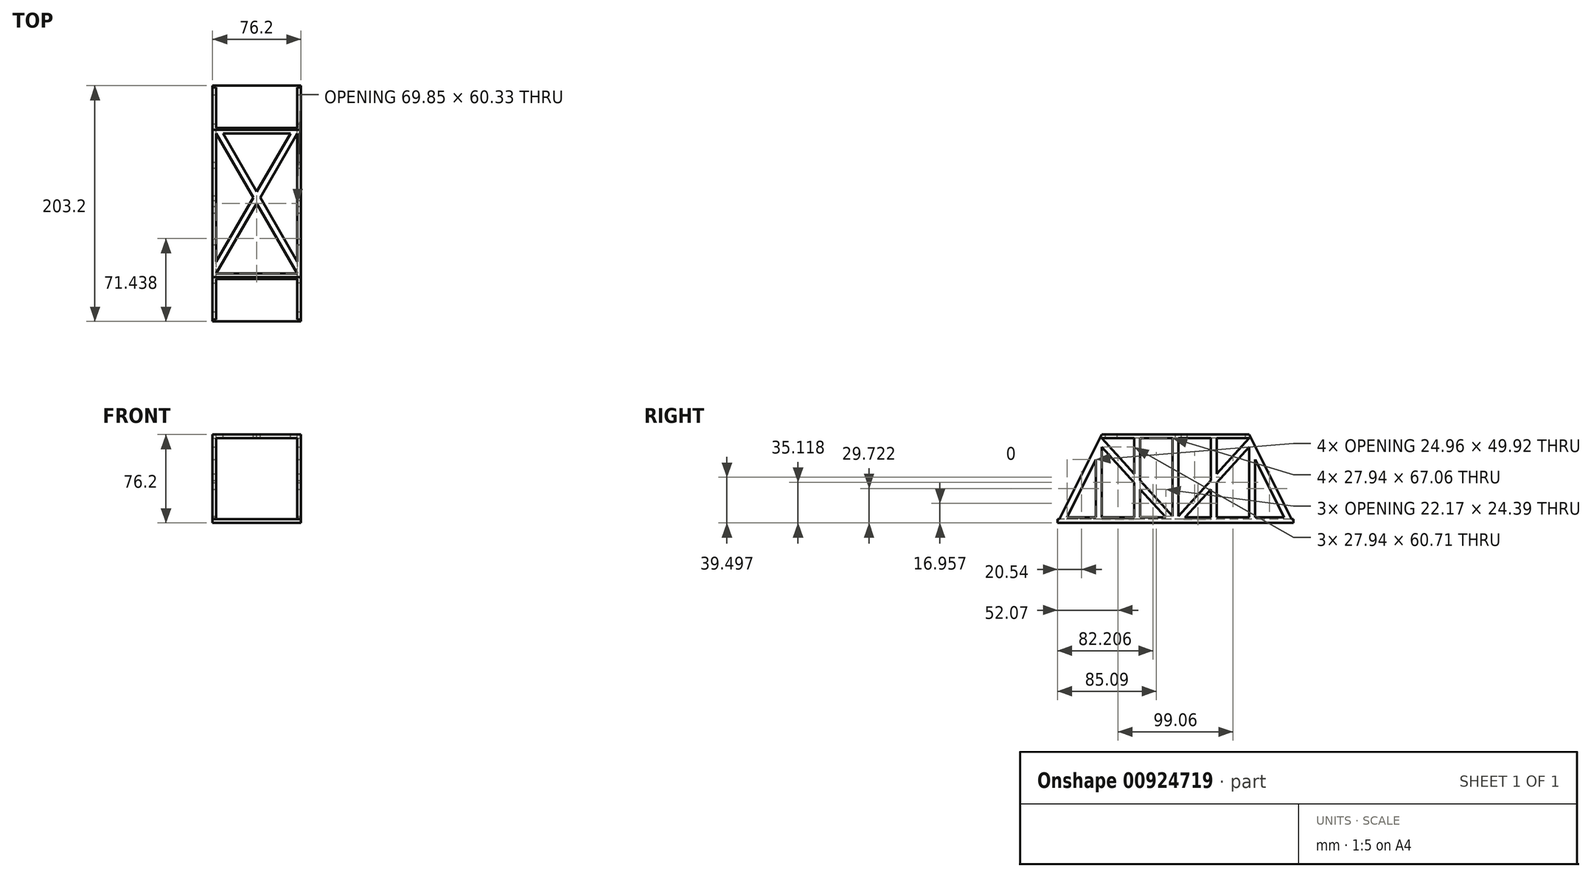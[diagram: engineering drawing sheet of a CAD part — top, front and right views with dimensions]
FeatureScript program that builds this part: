
annotation { "Feature Type Name" : "Feature", "Feature Type Description" : "" }
export const myFeature = defineFeature(function(context is Context, id is Id, definition is map)
    precondition{}
    {
        {
            var Q0;
            Q0=qCreatedBy(makeId("Right.planeOp"),FACE);
            var sketch = newSketch(context, id + "F0", { "sketchPlane" : qUnion([Q0])});
            skLineSegment(sketch, "E0", {"start": v(-101.6, -38.1) * mm, "end": v(101.6, -38.1) * mm});
            skLineSegment(sketch, "E1", {"start": v(-63.5, 38.1) * mm, "end": v(63.5, 38.1) * mm});
            skLineSegment(sketch, "E2", {"start": v(-101.6, -38.1) * mm, "end": v(-63.5, 38.1) * mm});
            skLineSegment(sketch, "E3", {"start": v(63.5, 38.1) * mm, "end": v(101.6, -38.1) * mm});
            skSolve(sketch);
        }
        {
            var Q0;
            Q0=qSketchRegion(id+"F0",true);
            extrude(context, id + "F1", {"entities" : qUnion([Q0]), "endBound" : BoundingType.SYMMETRIC, "depth" : 76.2 * mm, "offsetDistance" : 25.4 * mm});
        }
        {
            var Q0;
            Q0=makeQuery(id+"F1.opExtrude","CAP_FACE",FACE,{"disambiguationData":[OSD([sQuery(id+"F0.wireOp",EDGE,"E0"),sQuery(id+"F0.wireOp",EDGE,"E1"),sQuery(id+"F0.wireOp",EDGE,"E2"),sQuery(id+"F0.wireOp",EDGE,"E3")])],"isStart":false});
            var sketch = newSketch(context, id + "F2", { "sketchPlane" : qUnion([Q0])});
            skLineSegment(sketch, "E4", {"start": v(-63.5, 34.92) * mm, "end": v(-63.5, -34.93) * mm});
            skLineSegment(sketch, "E5", {"start": v(-63.5, -34.93) * mm, "end": v(63.5, -34.93) * mm});
            skLineSegment(sketch, "E6", {"start": v(63.5, -34.93) * mm, "end": v(63.5, 34.93) * mm});
            skLineSegment(sketch, "E7", {"start": v(63.5, 34.93) * mm, "end": v(-63.5, 34.92) * mm});
            skLineSegment(sketch, "E8", {"start": v(-63.5, 34.93) * mm, "end": v(0, -34.93) * mm});
            skLineSegment(sketch, "E9", {"start": v(0, -34.92) * mm, "end": v(63.5, 34.93) * mm});
            skLineSegment(sketch, "E10", {"start": v(-63.5, 27.37) * mm, "end": v(-6.87, -34.93) * mm});
            skLineSegment(sketch, "E11", {"start": v(63.5, 27.37) * mm, "end": v(6.87, -34.93) * mm});
            skLineSegment(sketch, "E12", {"start": v(-68.58, 16.58) * mm, "end": v(-68.58, -34.93) * mm});
            skLineSegment(sketch, "E13", {"start": v(-68.58, 16.58) * mm, "end": v(-94.33, -34.93) * mm});
            skLineSegment(sketch, "E14", {"start": v(-94.33, -34.93) * mm, "end": v(-68.58, -34.93) * mm});
            skLineSegment(sketch, "E15.MirrorCS", {"start": v(68.58, 16.58) * mm, "end": v(68.58, -34.93) * mm});
            skLineSegment(sketch, "E16.MirrorCS", {"start": v(68.58, 16.58) * mm, "end": v(94.33, -34.93) * mm});
            skLineSegment(sketch, "E17.MirrorCS", {"start": v(94.33, -34.93) * mm, "end": v(68.58, -34.93) * mm});
            skLineSegment(sketch, "E18.bottom", {"start": v(2.54, -34.93) * mm, "end": v(-2.54, -34.93) * mm});
            skLineSegment(sketch, "E18.top", {"start": v(2.54, 34.93) * mm, "end": v(-2.54, 34.93) * mm});
            skLineSegment(sketch, "E18.left", {"start": v(2.54, -34.92) * mm, "end": v(2.54, 34.92) * mm});
            skLineSegment(sketch, "E18.right", {"start": v(-2.54, -34.92) * mm, "end": v(-2.54, 34.92) * mm});
            skPoint(sketch, "E18.middle", {"position": v(0, 0) * mm});
            skLineSegment(sketch, "E19.bottom", {"start": v(-30.48, -34.93) * mm, "end": v(-35.56, -34.93) * mm});
            skLineSegment(sketch, "E19.top", {"start": v(-30.48, 34.93) * mm, "end": v(-35.56, 34.93) * mm});
            skLineSegment(sketch, "E19.left", {"start": v(-30.48, -34.93) * mm, "end": v(-30.48, 34.93) * mm});
            skLineSegment(sketch, "E19.right", {"start": v(-35.56, -34.93) * mm, "end": v(-35.56, 34.93) * mm});
            skPoint(sketch, "E19.middle", {"position": v(-33.02, 0) * mm});
            skLineSegment(sketch, "E20.MirrorCS", {"start": v(35.56, -34.93) * mm, "end": v(35.56, 34.93) * mm});
            skLineSegment(sketch, "E21.MirrorCS", {"start": v(30.48, -34.93) * mm, "end": v(30.48, 34.93) * mm});
            skSolve(sketch);
        }
        {
            var Q0;
            Q0=qCreatedBy(makeId("Front.planeOp"),FACE);
            var sketch = newSketch(context, id + "F3", { "sketchPlane" : qUnion([Q0])});
            skLineSegment(sketch, "E22.bottom", {"start": v(34.93, -34.93) * mm, "end": v(-34.93, -34.93) * mm});
            skLineSegment(sketch, "E22.top", {"start": v(34.93, 34.93) * mm, "end": v(-34.93, 34.93) * mm});
            skLineSegment(sketch, "E22.left", {"start": v(34.93, -34.93) * mm, "end": v(34.93, 34.93) * mm});
            skLineSegment(sketch, "E22.right", {"start": v(-34.93, -34.93) * mm, "end": v(-34.93, 34.93) * mm});
            skPoint(sketch, "E22.middle", {"position": v(0, 0) * mm});
            skSolve(sketch);
        }
        {
            var Q0;
            Q0=qSketchRegion(id+"F3",true);
            extrude(context, id + "F4", {"entities" : qUnion([Q0]), "operationType" : NewBodyOperationType.REMOVE, "endBound" : BoundingType.SYMMETRIC, "oppositeDirection" : true, "depth" : 254 * mm, "offsetDistance" : 25.4 * mm});
        }
        {
            var Q0;
            Q0=makeQuery(id+"F2.imprint","IMPRINT",FACE,{"disambiguationData":[TD([[makeQuery(id+"F2.imprint","IMPRINT",EDGE,{"derivedFrom":sQuery(id+"F2.wireOp",EDGE,"E12")}),-1.0]])]});
            var Q1;
            {var subQ3=sQuery(id+"F2.wireOp",EDGE,"E10");Q1=makeQuery(id+"F2.imprint","IMPRINT",FACE,{"disambiguationData":[TD([[makeQuery(id+"F2.imprint","IMPRINT",EDGE,{"derivedFrom":subQ3}),-1.0]])]});}
            var Q2;
            {var subQ0=sQuery(id+"F2.wireOp",EDGE,"E8");var subQ3=sQuery(id+"F2.wireOp",EDGE,"E18.right");var subQ5=makeQuery(id+"F2.imprint","INTERSECT",VERTEX,{"derivedFrom":[subQ0,subQ3]});Q2=makeQuery(id+"F2.imprint","IMPRINT",FACE,{"disambiguationData":[TD([[makeQuery(id+"F2.imprint","IMPRINT",EDGE,{"disambiguationData":[TD([[subQ5,1.0]])],"derivedFrom":subQ0}),1.0]])]});}
            var Q3;
            {var subQ0=sQuery(id+"F2.wireOp",EDGE,"E9");var subQ3=sQuery(id+"F2.wireOp",EDGE,"E18.left");var subQ5=makeQuery(id+"F2.imprint","INTERSECT",VERTEX,{"derivedFrom":[subQ0,subQ3]});Q3=makeQuery(id+"F2.imprint","IMPRINT",FACE,{"disambiguationData":[TD([[makeQuery(id+"F2.imprint","IMPRINT",EDGE,{"disambiguationData":[TD([[subQ5,-1.0]])],"derivedFrom":subQ0}),1.0]])]});}
            var Q4;
            {var subQ3=sQuery(id+"F2.wireOp",EDGE,"E11");Q4=makeQuery(id+"F2.imprint","IMPRINT",FACE,{"disambiguationData":[TD([[makeQuery(id+"F2.imprint","IMPRINT",EDGE,{"derivedFrom":subQ3}),1.0]])]});}
            var Q5;
            Q5=makeQuery(id+"F2.imprint","IMPRINT",FACE,{"disambiguationData":[TD([[makeQuery(id+"F2.imprint","IMPRINT",EDGE,{"derivedFrom":sQuery(id+"F2.wireOp",EDGE,"E15.MirrorCS")}),1.0]])]});
            var Q6;
            {var subQ0=sQuery(id+"F2.wireOp",EDGE,"E5");var subQ1=sQuery(id+"F2.wireOp",EDGE,"E4");var subQ2=makeQuery(id+"F2.imprint","INTERSECT",VERTEX,{"derivedFrom":[subQ1,subQ0]});Q6=makeQuery(id+"F2.imprint","IMPRINT",FACE,{"disambiguationData":[TD([[makeQuery(id+"F2.imprint","IMPRINT",EDGE,{"disambiguationData":[TD([[subQ2,1.0]])],"derivedFrom":subQ1}),1.0]])]});}
            var Q7;
            {var subQ0=sQuery(id+"F2.wireOp",EDGE,"E8");var subQ3=sQuery(id+"F2.wireOp",EDGE,"E19.right");var subQ5=makeQuery(id+"F2.imprint","INTERSECT",VERTEX,{"derivedFrom":[subQ0,subQ3]});Q7=makeQuery(id+"F2.imprint","IMPRINT",FACE,{"disambiguationData":[TD([[makeQuery(id+"F2.imprint","IMPRINT",EDGE,{"disambiguationData":[TD([[subQ5,1.0]])],"derivedFrom":subQ0}),1.0]])]});}
            var Q8;
            {var subQ1=sQuery(id+"F2.wireOp",EDGE,"E7");var subQ3=sQuery(id+"F2.wireOp",EDGE,"E20.MirrorCS");var subQ4=makeQuery(id+"F2.imprint","INTERSECT",VERTEX,{"derivedFrom":[subQ1,subQ3]});Q8=makeQuery(id+"F2.imprint","IMPRINT",FACE,{"disambiguationData":[TD([[makeQuery(id+"F2.imprint","IMPRINT",EDGE,{"disambiguationData":[TD([[subQ4,1.0]])],"derivedFrom":subQ3}),-1.0]])]});}
            var Q9;
            {var subQ0=sQuery(id+"F2.wireOp",EDGE,"E6");var subQ1=sQuery(id+"F2.wireOp",EDGE,"E5");var subQ2=makeQuery(id+"F2.imprint","INTERSECT",VERTEX,{"derivedFrom":[subQ1,subQ0]});Q9=makeQuery(id+"F2.imprint","IMPRINT",FACE,{"disambiguationData":[TD([[makeQuery(id+"F2.imprint","IMPRINT",EDGE,{"disambiguationData":[TD([[subQ2,1.0]])],"derivedFrom":subQ1}),1.0]])]});}
            extrude(context, id + "F5", {"entities" : qUnion([Q0, Q1, Q2, Q3, Q4, Q5, Q6, Q7, Q8, Q9]), "operationType" : NewBodyOperationType.REMOVE, "oppositeDirection" : true, "depth" : 101.6 * mm, "offsetDistance" : 25.4 * mm});
        }
        {
            var Q0;
            Q0=makeQuery(id+"F1.opExtrude","SWEPT_FACE",FACE,{"disambiguationData":[OSD([sQuery(id+"F0.wireOp",EDGE,"E1")])]});
            var sketch = newSketch(context, id + "F6", { "sketchPlane" : qUnion([Q0])});
            skLineSegment(sketch, "E23.bottom", {"start": v(34.92, -60.32) * mm, "end": v(-34.92, -60.32) * mm});
            skLineSegment(sketch, "E23.top", {"start": v(34.92, 60.33) * mm, "end": v(-34.92, 60.32) * mm});
            skLineSegment(sketch, "E23.left", {"start": v(34.92, -60.33) * mm, "end": v(34.92, 60.33) * mm});
            skLineSegment(sketch, "E23.right", {"start": v(-34.92, -60.33) * mm, "end": v(-34.92, 60.33) * mm});
            skPoint(sketch, "E23.middle", {"position": v(0, 0) * mm});
            skLineSegment(sketch, "E24", {"start": v(-34.92, 60.32) * mm, "end": v(34.92, -60.32) * mm});
            skLineSegment(sketch, "E25", {"start": v(34.92, 60.33) * mm, "end": v(-34.92, -60.32) * mm});
            skLineSegment(sketch, "E26", {"start": v(-34.92, -50.19) * mm, "end": v(29.06, 60.32) * mm});
            skLineSegment(sketch, "E27", {"start": v(-29.06, 60.33) * mm, "end": v(34.92, -50.19) * mm});
            skSolve(sketch);
        }
        {
            var Q0;
            {var subQ0=sQuery(id+"F6.wireOp",EDGE,"E26");var subQ1=sQuery(id+"F6.wireOp",EDGE,"E23.top");var subQ2=makeQuery(id+"F6.imprint","INTERSECT",VERTEX,{"derivedFrom":[subQ1,subQ0]});Q0=makeQuery(id+"F6.imprint","IMPRINT",FACE,{"disambiguationData":[TD([[makeQuery(id+"F6.imprint","IMPRINT",EDGE,{"disambiguationData":[TD([[subQ2,-1.0]])],"derivedFrom":subQ1}),1.0]])]});}
            var Q1;
            {var subQ1=sQuery(id+"F6.wireOp",EDGE,"E23.right");var subQ3=sQuery(id+"F6.wireOp",EDGE,"E26");var subQ4=makeQuery(id+"F6.imprint","INTERSECT",VERTEX,{"derivedFrom":[subQ1,subQ3]});Q1=makeQuery(id+"F6.imprint","IMPRINT",FACE,{"disambiguationData":[TD([[makeQuery(id+"F6.imprint","IMPRINT",EDGE,{"disambiguationData":[TD([[subQ4,-1.0]])],"derivedFrom":subQ3}),1.0]])]});}
            var Q2;
            {var subQ1=sQuery(id+"F6.wireOp",EDGE,"E23.left");var subQ3=sQuery(id+"F6.wireOp",EDGE,"E27");var subQ4=makeQuery(id+"F6.imprint","INTERSECT",VERTEX,{"derivedFrom":[subQ1,subQ3]});Q2=makeQuery(id+"F6.imprint","IMPRINT",FACE,{"disambiguationData":[TD([[makeQuery(id+"F6.imprint","IMPRINT",EDGE,{"disambiguationData":[TD([[subQ4,1.0]])],"derivedFrom":subQ3}),1.0]])]});}
            var Q3;
            {var subQ0=sQuery(id+"F6.wireOp",EDGE,"E23.bottom");Q3=makeQuery(id+"F6.imprint","IMPRINT",FACE,{"disambiguationData":[TD([[makeQuery(id+"F6.imprint","IMPRINT",EDGE,{"derivedFrom":subQ0}),-1.0]])]});}
            extrude(context, id + "F7", {"entities" : qUnion([Q0, Q1, Q2, Q3]), "operationType" : NewBodyOperationType.REMOVE, "oppositeDirection" : true, "depth" : 3.17 * mm, "offsetDistance" : 25.4 * mm});
        }
        {
            var Q0;
            {var subQ0=sQuery(id+"F2.wireOp",EDGE,"E5");Q0=makeQuery(id+"F5.boolean.opBoolean","MERGE",FACE,{"derivedFrom":[makeQuery(id+"F4.boolean.opBoolean","COPY",FACE,{"derivedFrom":makeQuery(id+"F4.opExtrude","SWEPT_FACE",FACE,{"disambiguationData":[OSD([sQuery(id+"F3.wireOp",EDGE,"E22.bottom")])]})})],"fromTools":[makeQuery(id+"F5.opExtrude","SWEPT_FACE",FACE,{"disambiguationData":[OSD([subQ0]),TDD([makeQuery(id+"F2.imprint","IMPRINT",EDGE,{"disambiguationData":[TD([[makeQuery(id+"F2.imprint","INTERSECT",VERTEX,{"derivedFrom":[sQuery(id+"F2.wireOp",EDGE,"E4"),subQ0]}),-1.0]])],"derivedFrom":subQ0})])]}),makeQuery(id+"F5.opExtrude","SWEPT_FACE",FACE,{"disambiguationData":[OSD([subQ0]),TDD([makeQuery(id+"F2.imprint","IMPRINT",EDGE,{"disambiguationData":[TD([[makeQuery(id+"F2.imprint","INTERSECT",VERTEX,{"derivedFrom":[subQ0,sQuery(id+"F2.wireOp",EDGE,"E6")]}),1.0]])],"derivedFrom":subQ0})])]}),makeQuery(id+"F5.opExtrude","SWEPT_FACE",FACE,{"disambiguationData":[OSD([sQuery(id+"F2.wireOp",EDGE,"E14")])]}),makeQuery(id+"F5.opExtrude","SWEPT_FACE",FACE,{"disambiguationData":[OSD([sQuery(id+"F2.wireOp",EDGE,"E17.MirrorCS")])]})]});}
            var sketch = newSketch(context, id + "F8", { "sketchPlane" : qUnion([Q0])});
            skLineSegment(sketch, "E28.bottom", {"start": v(38.1, -94.33) * mm, "end": v(34.92, -94.33) * mm});
            skLineSegment(sketch, "E28.top", {"start": v(38.1, 94.33) * mm, "end": v(34.92, 94.33) * mm});
            skLineSegment(sketch, "E28.left", {"start": v(38.1, -94.33) * mm, "end": v(38.1, 94.33) * mm});
            skLineSegment(sketch, "E28.right", {"start": v(34.92, -94.33) * mm, "end": v(34.92, 94.33) * mm});
            skLineSegment(sketch, "E29.MirrorCS", {"start": v(-38.1, -94.33) * mm, "end": v(-38.1, 94.33) * mm});
            skLineSegment(sketch, "E30.MirrorCS", {"start": v(-34.92, -94.33) * mm, "end": v(-34.92, 94.33) * mm});
            skSolve(sketch);
        }
        {
            var Q0;
            Q0=qSketchRegion(id+"F8",true);
            var Q1;
            {var subQ3=sQuery(id+"F3.wireOp",EDGE,"E22.right");var subQ4=makeQuery(id+"F4.boolean.opBoolean","COPY",FACE,{"derivedFrom":makeQuery(id+"F4.opExtrude","SWEPT_FACE",FACE,{"disambiguationData":[OSD([subQ3])]})});var subQ7=sQuery(id+"F2.wireOp",EDGE,"E12");var subQ11=sQuery(id+"F2.wireOp",EDGE,"E14");var subQ14=makeQuery(id+"F5.boolean.opBoolean","COPY",EDGE,{"disambiguationData":[TD([subQ4])],"derivedFrom":makeQuery(id+"F5.opExtrude","SWEPT_EDGE",EDGE,{"disambiguationData":[OSD([subQ7,subQ11])]})});Q1=makeQuery(id+"F8.imprint","IMPRINT",FACE,{"disambiguationData":[TD([[makeQuery(id+"F8.imprint","IMPRINT",EDGE,{"derivedFrom":subQ14}),-1.0]])]});}
            var Q2;
            {var subQ3=makeQuery(id+"F4.boolean.opBoolean","COPY",FACE,{"derivedFrom":makeQuery(id+"F4.opExtrude","SWEPT_FACE",FACE,{"disambiguationData":[OSD([sQuery(id+"F3.wireOp",EDGE,"E22.right")])]})});var subQ6=sQuery(id+"F2.wireOp",EDGE,"E5");var subQ7=sQuery(id+"F2.wireOp",EDGE,"E10");var subQ12=makeQuery(id+"F5.boolean.opBoolean","COPY",EDGE,{"disambiguationData":[TD([subQ3])],"derivedFrom":makeQuery(id+"F5.opExtrude","SWEPT_EDGE",EDGE,{"disambiguationData":[OSD([subQ6,subQ7])]})});Q2=makeQuery(id+"F8.imprint","IMPRINT",FACE,{"disambiguationData":[TD([[makeQuery(id+"F8.imprint","IMPRINT",EDGE,{"derivedFrom":subQ12}),-1.0]])]});}
            var Q3;
            {var subQ1=sQuery(id+"F2.wireOp",EDGE,"E5");var subQ3=makeQuery(id+"F4.boolean.opBoolean","COPY",FACE,{"derivedFrom":makeQuery(id+"F4.opExtrude","SWEPT_FACE",FACE,{"disambiguationData":[OSD([sQuery(id+"F3.wireOp",EDGE,"E22.right")])]})});var subQ5=sQuery(id+"F2.wireOp",EDGE,"E6");var subQ11=makeQuery(id+"F5.boolean.opBoolean","COPY",EDGE,{"disambiguationData":[TD([subQ3])],"derivedFrom":makeQuery(id+"F5.opExtrude","SWEPT_EDGE",EDGE,{"disambiguationData":[OSD([subQ1,subQ5])]})});Q3=makeQuery(id+"F8.imprint","IMPRINT",FACE,{"disambiguationData":[TD([[makeQuery(id+"F8.imprint","IMPRINT",EDGE,{"derivedFrom":subQ11}),-1.0]])]});}
            var Q4;
            {var subQ3=sQuery(id+"F3.wireOp",EDGE,"E22.right");var subQ4=makeQuery(id+"F4.boolean.opBoolean","COPY",FACE,{"derivedFrom":makeQuery(id+"F4.opExtrude","SWEPT_FACE",FACE,{"disambiguationData":[OSD([subQ3])]})});var subQ11=sQuery(id+"F2.wireOp",EDGE,"E15.MirrorCS");var subQ12=sQuery(id+"F2.wireOp",EDGE,"E17.MirrorCS");var subQ14=makeQuery(id+"F5.boolean.opBoolean","COPY",EDGE,{"disambiguationData":[TD([subQ4])],"derivedFrom":makeQuery(id+"F5.opExtrude","SWEPT_EDGE",EDGE,{"disambiguationData":[OSD([subQ11,subQ12])]})});Q4=makeQuery(id+"F8.imprint","IMPRINT",FACE,{"disambiguationData":[TD([[makeQuery(id+"F8.imprint","IMPRINT",EDGE,{"derivedFrom":subQ14}),1.0]])]});}
            extrude(context, id + "F9", {"entities" : qUnion([Q0, Q1, Q2, Q3, Q4]), "operationType" : NewBodyOperationType.ADD, "depth" : 1.59 * mm, "offsetDistance" : 25.4 * mm});
        }
        {
            var Q0;
            Q0=makeQuery(id+"F9.boolean.opBoolean","MERGE",FACE,{"derivedFrom":[makeQuery(id+"F1.opExtrude","CAP_FACE",FACE,{"disambiguationData":[OSD([sQuery(id+"F0.wireOp",EDGE,"E0"),sQuery(id+"F0.wireOp",EDGE,"E1"),sQuery(id+"F0.wireOp",EDGE,"E2"),sQuery(id+"F0.wireOp",EDGE,"E3")])],"isStart":false}),makeQuery(id+"F9.opExtrude","SWEPT_FACE",FACE,{"disambiguationData":[OSD([sQuery(id+"F8.wireOp",EDGE,"E28.left")])]})]});
            var sketch = newSketch(context, id + "F10", { "sketchPlane" : qUnion([Q0])});
            skLineSegment(sketch, "E31.bottom", {"start": v(-101.6, -38.1) * mm, "end": v(-95.64, -38.1) * mm});
            skLineSegment(sketch, "E31.top", {"start": v(-101.6, -34.92) * mm, "end": v(-95.64, -34.92) * mm});
            skLineSegment(sketch, "E31.left", {"start": v(-101.6, -38.1) * mm, "end": v(-101.6, -34.92) * mm});
            skLineSegment(sketch, "E31.right", {"start": v(-95.64, -38.1) * mm, "end": v(-95.64, -34.92) * mm});
            skLineSegment(sketch, "E32.MirrorCS", {"start": v(101.6, -38.1) * mm, "end": v(101.6, -34.92) * mm});
            skLineSegment(sketch, "E33.MirrorCS", {"start": v(101.6, -34.92) * mm, "end": v(95.64, -34.92) * mm});
            skLineSegment(sketch, "E34.MirrorCS", {"start": v(95.64, -38.1) * mm, "end": v(95.64, -34.92) * mm});
            skLineSegment(sketch, "E35.MirrorCS", {"start": v(101.6, -38.1) * mm, "end": v(95.64, -38.1) * mm});
            skSolve(sketch);
        }
        {
            var Q0;
            Q0=qSketchRegion(id+"F10",true);
            extrude(context, id + "F11", {"entities" : qUnion([Q0]), "operationType" : NewBodyOperationType.ADD, "oppositeDirection" : true, "depth" : 76.2 * mm, "offsetDistance" : 25.4 * mm});
        }
    });
